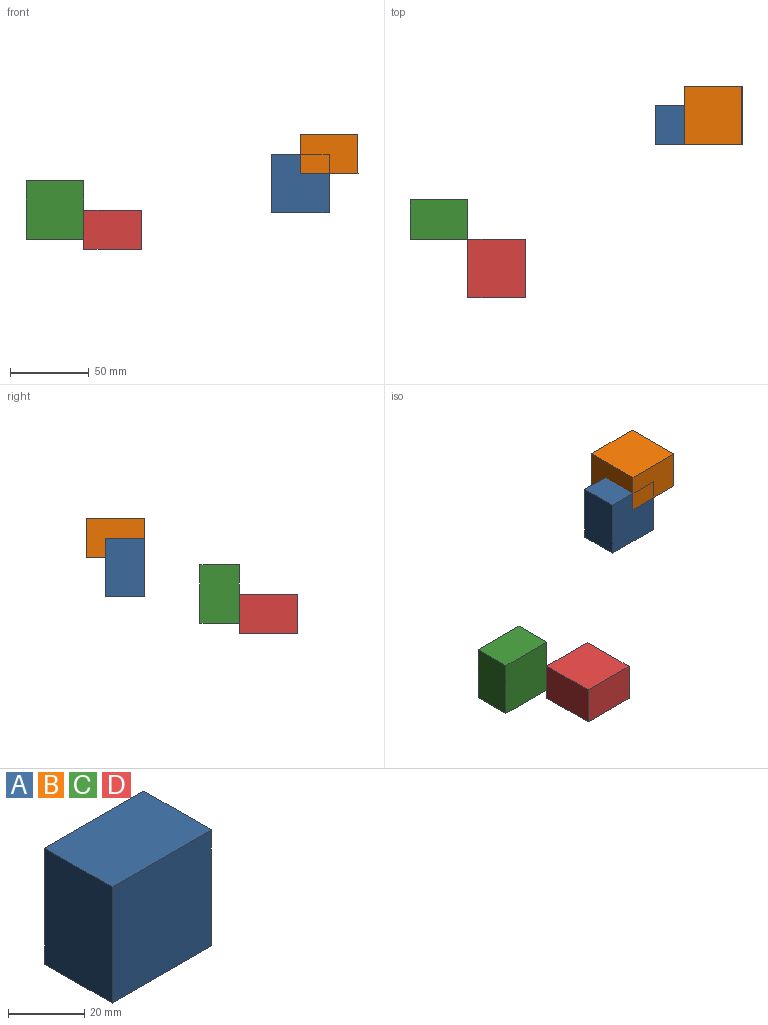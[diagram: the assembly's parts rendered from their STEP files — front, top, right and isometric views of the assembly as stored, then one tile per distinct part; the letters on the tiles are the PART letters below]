
ASSEMBLY  parts=4 mates=2
PART A: 6 faces, bbox 36.8x25x37.3 mm
  f0: plane 36.82x25mm, normal (0,0,1), area 920.5mm2, adj f1,f3,f4,f5
  f1: plane 37.3x25mm, normal (-1,0,0), area 932.4mm2, adj f0,f2,f4,f5
  f2: plane 36.82x25mm, normal (0,0,-1), area 920.5mm2, adj f1,f3,f4,f5
  f3: plane 37.3x25mm, normal (1,0,0), area 932.4mm2, adj f0,f2,f4,f5
  f4: plane 37.3x36.82mm, normal (0,-1,0), area 1373.4mm2, adj f0,f1,f2,f3
  f5: plane 37.3x36.82mm, normal (0,1,0), area 1373.4mm2, adj f0,f1,f2,f3
PART B: same geometry as A
PART C: same geometry as A
PART D: same geometry as A
PLACE A t=(129.16,52.54,-20.71)mm
PLACE B rot(axis=(1,0,0),90deg) t=(147.57,105.81,70.06)mm
PLACE C t=(-27.06,-7.63,-37.62)mm
PLACE D rot(axis=(-1,0,0),90deg) t=(9.76,-110.9,-3)mm
MATE revolute B.f0 <-> A.f4  axis (0,-1,0) through (71.15,27.54,57.56)mm
MATE revolute D.f0 <-> C.f4  axis (0,-1,0) through (-85.07,-32.63,22)mm
